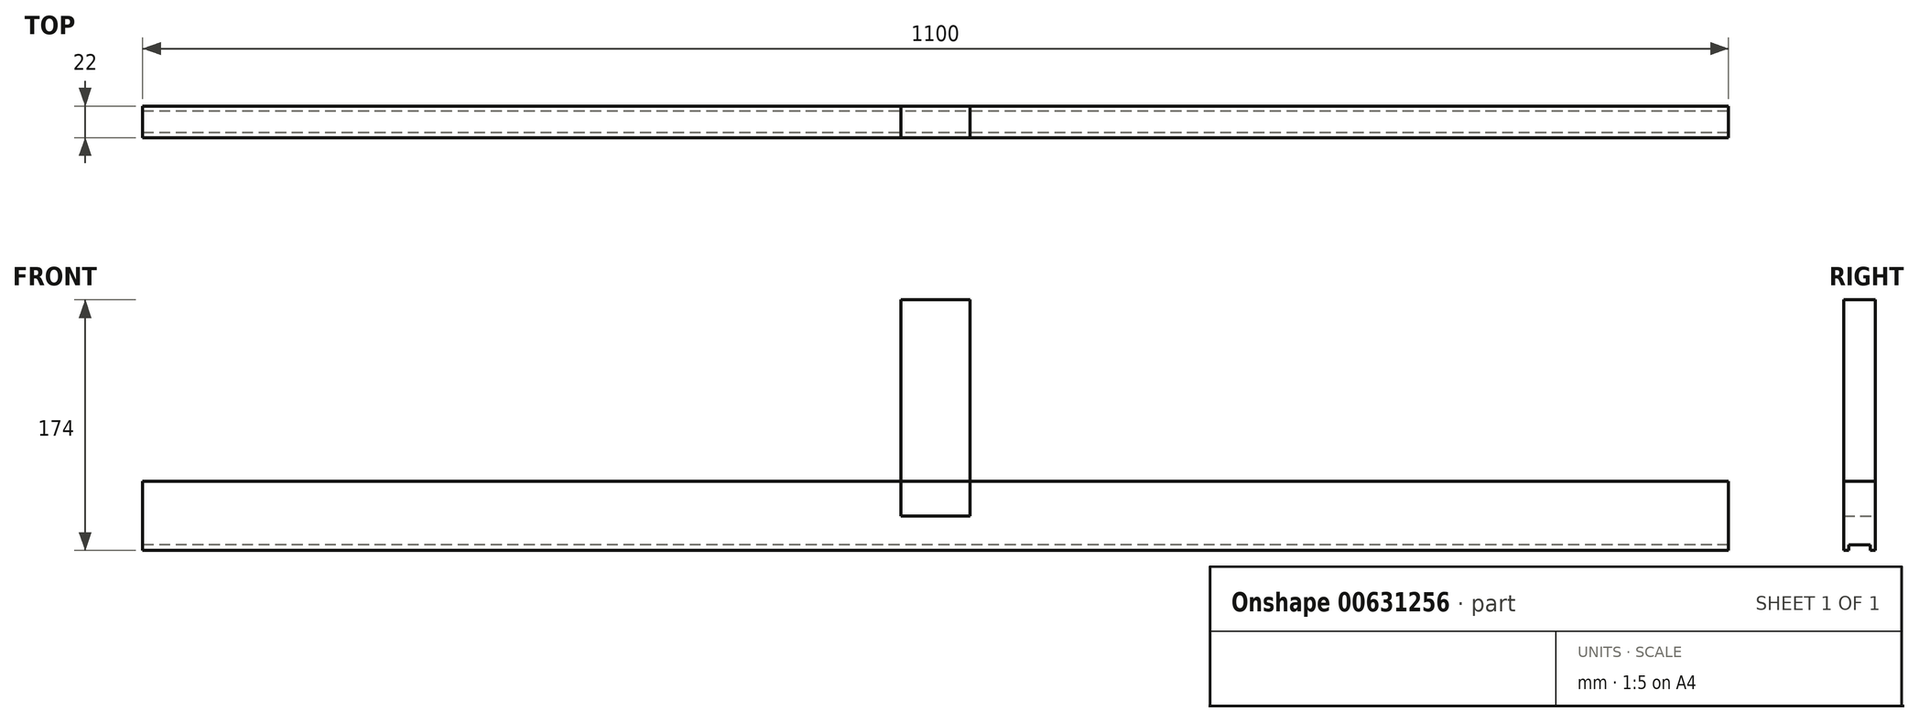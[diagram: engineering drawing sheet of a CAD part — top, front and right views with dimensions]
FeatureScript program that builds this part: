
annotation { "Feature Type Name" : "Feature", "Feature Type Description" : "" }
export const myFeature = defineFeature(function(context is Context, id is Id, definition is map)
    precondition{}
    {
        {
            var Q0;
            Q0=qCreatedBy(makeId("Top.planeOp"),FACE);
            var sketch = newSketch(context, id + "F0", { "sketchPlane" : qUnion([Q0])});
            skLineSegment(sketch, "E0.bottom", {"start": v(550, -11) * mm, "end": v(-550, -11) * mm});
            skLineSegment(sketch, "E0.top", {"start": v(550, 11) * mm, "end": v(-550, 11) * mm});
            skLineSegment(sketch, "E0.left", {"start": v(550, -11) * mm, "end": v(550, 11) * mm});
            skLineSegment(sketch, "E0.right", {"start": v(-550, -11) * mm, "end": v(-550, 11) * mm});
            skPoint(sketch, "E0.middle", {"position": v(0, 0) * mm});
            skSolve(sketch);
        }
        {
            var Q0;
            Q0 = qSketchRegion(id + "F0", true);
            extrude(context, id + "F1", {"entities" : qUnion([Q0]), "depth" : 48 * mm, "offsetDistance" : 25 * mm});
        }
        {
            var Q0;
            Q0=makeQuery(id+"F1.opExtrude","CAP_FACE",FACE,{"disambiguationData":[OSD([sQuery(id+"F0.wireOp",EDGE,"E0.bottom"),sQuery(id+"F0.wireOp",EDGE,"E0.top"),sQuery(id+"F0.wireOp",EDGE,"E0.left"),sQuery(id+"F0.wireOp",EDGE,"E0.right")])],"isStart":false});
            var sketch = newSketch(context, id + "F2", { "sketchPlane" : qUnion([Q0])});
            skLineSegment(sketch, "E1.bottom", {"start": v(24, -11) * mm, "end": v(-24, -11) * mm});
            skLineSegment(sketch, "E1.top", {"start": v(24, 11) * mm, "end": v(-24, 11) * mm});
            skLineSegment(sketch, "E1.left", {"start": v(24, -11) * mm, "end": v(24, 11) * mm});
            skLineSegment(sketch, "E1.right", {"start": v(-24, -11) * mm, "end": v(-24, 11) * mm});
            skPoint(sketch, "E1.middle", {"position": v(0, 0) * mm});
            skSolve(sketch);
        }
        {
            var Q0;
            Q0 = qSketchRegion(id + "F2", true);
            extrude(context, id + "F3", {"entities" : qUnion([Q0]), "depth" : (150 - 24) * mm, "offsetDistance" : 25 * mm, "hasSecondDirection" : true, "secondDirectionOppositeDirection" : true, "secondDirectionDepth" : (48 / 2) * mm});
        }
        {
            var Q0;
            Q0=makeQuery(id+"F1.opExtrude","CAP_FACE",FACE,{"disambiguationData":[OSD([sQuery(id+"F0.wireOp",EDGE,"E0.bottom"),sQuery(id+"F0.wireOp",EDGE,"E0.top"),sQuery(id+"F0.wireOp",EDGE,"E0.left"),sQuery(id+"F0.wireOp",EDGE,"E0.right")])],"isStart":true});
            var sketch = newSketch(context, id + "F4", { "sketchPlane" : qUnion([Q0])});
            skLineSegment(sketch, "E2.bottom", {"start": v(550, -7.5) * mm, "end": v(-550, -7.5) * mm});
            skLineSegment(sketch, "E2.top", {"start": v(550, 7.5) * mm, "end": v(-550, 7.5) * mm});
            skLineSegment(sketch, "E2.left", {"start": v(550, -7.5) * mm, "end": v(550, 7.5) * mm});
            skLineSegment(sketch, "E2.right", {"start": v(-550, -7.5) * mm, "end": v(-550, 7.5) * mm});
            skPoint(sketch, "E2.middle", {"position": v(0, 0) * mm});
            skSolve(sketch);
        }
        {
            var Q0;
            Q0 = qSketchRegion(id + "F4", true);
            extrude(context, id + "F5", {"entities" : qUnion([Q0]), "operationType" : NewBodyOperationType.REMOVE, "oppositeDirection" : true, "depth" : 4 * mm, "offsetDistance" : 25 * mm});
        }
    });
